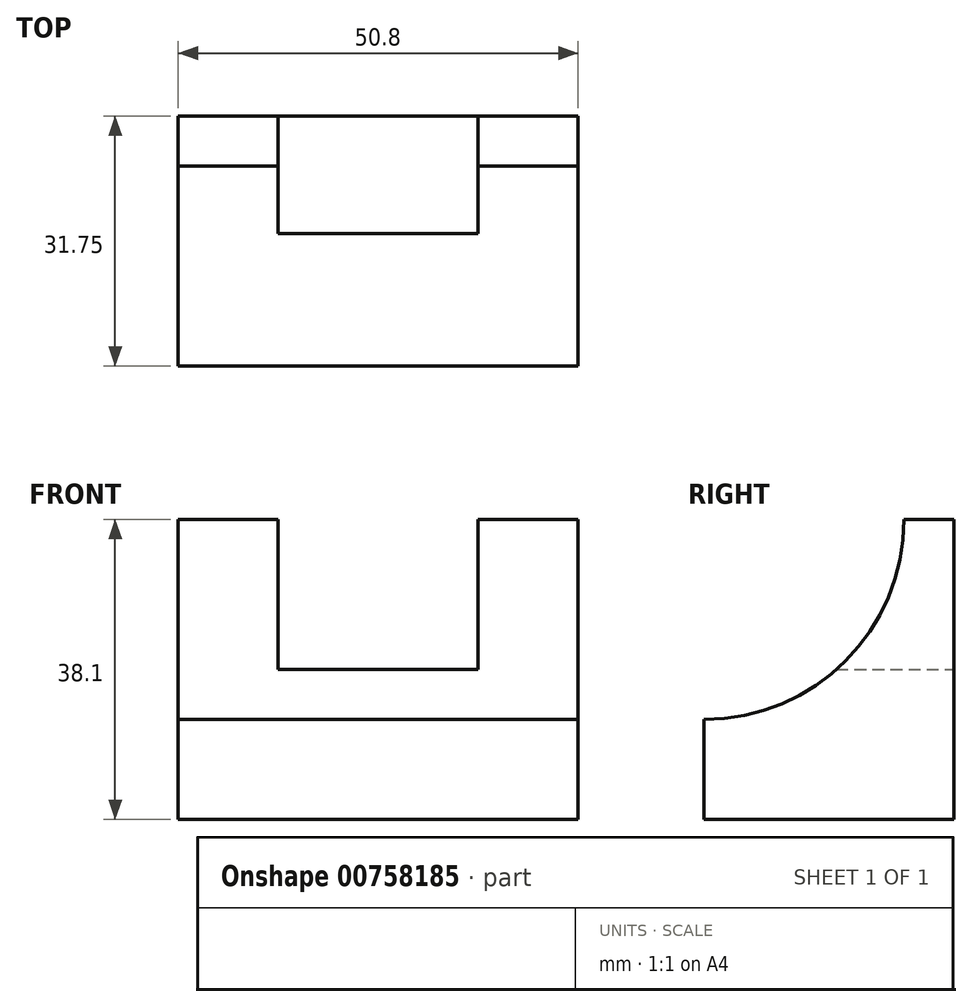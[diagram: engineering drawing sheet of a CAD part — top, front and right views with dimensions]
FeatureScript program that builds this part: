
annotation { "Feature Type Name" : "Feature", "Feature Type Description" : "" }
export const myFeature = defineFeature(function(context is Context, id is Id, definition is map)
    precondition{}
    {
        {
            var Q0;
            Q0=qCreatedBy(makeId("Front.planeOp"),FACE);
            var sketch = newSketch(context, id + "F0", { "sketchPlane" : qUnion([Q0])});
            skLineSegment(sketch, "E0", {"start": v(0, 0) * mm, "end": v(50.8, 0) * mm});
            skLineSegment(sketch, "E1", {"start": v(50.8, 0) * mm, "end": v(50.8, 38.1) * mm});
            skLineSegment(sketch, "E2", {"start": v(50.8, 38.1) * mm, "end": v(0, 38.1) * mm});
            skLineSegment(sketch, "E3", {"start": v(0, 38.1) * mm, "end": v(0, 0) * mm});
            skSolve(sketch);
        }
        {
            var Q0;
            Q0 = qSketchRegion(id + "F0", true);
            extrude(context, id + "F1", {"entities" : qUnion([Q0]), "oppositeDirection" : true, "depth" : 31.75 * mm, "offsetDistance" : 25.4 * mm});
        }
        {
            var Q0;
            Q0=makeQuery(id+"F1.opExtrude","SWEPT_FACE",FACE,{"disambiguationData":[OSD([sQuery(id+"F0.wireOp",EDGE,"E1")])]});
            var sketch = newSketch(context, id + "F2", { "sketchPlane" : qUnion([Q0])});
            skArc(sketch, "E4", {"start": v(0, 12.7) * mm, "mid": v(17.96, 20.14) * mm, "end": v(25.4, 38.1) * mm});
            skSolve(sketch);
        }
        {
            var Q0;
            Q0 = qSketchRegion(id + "F2", true);
            var Q1;
            {var subQ0=sQuery(id+"F2.wireOp",EDGE,"E4");Q1=makeQuery(id+"F2.imprint","IMPRINT",FACE,{"disambiguationData":[TD([[makeQuery(id+"F2.imprint","IMPRINT",EDGE,{"derivedFrom":subQ0}),1.0]])]});}
            extrude(context, id + "F3", {"entities" : qUnion([Q0, Q1]), "operationType" : NewBodyOperationType.REMOVE, "oppositeDirection" : true, "depth" : 50.8 * mm, "offsetDistance" : 25.4 * mm});
        }
        {
            var Q0;
            Q0=makeQuery(id+"F1.opExtrude","CAP_FACE",FACE,{"disambiguationData":[OSD([sQuery(id+"F0.wireOp",EDGE,"E0"),sQuery(id+"F0.wireOp",EDGE,"E1"),sQuery(id+"F0.wireOp",EDGE,"E2"),sQuery(id+"F0.wireOp",EDGE,"E3")])],"isStart":false});
            var sketch = newSketch(context, id + "F4", { "sketchPlane" : qUnion([Q0])});
            skLineSegment(sketch, "E5", {"start": v(-38.1, 38.1) * mm, "end": v(-38.1, 19.05) * mm});
            skLineSegment(sketch, "E6", {"start": v(-38.1, 19.05) * mm, "end": v(-12.7, 19.05) * mm});
            skLineSegment(sketch, "E7", {"start": v(-12.7, 19.05) * mm, "end": v(-12.7, 38.1) * mm});
            skSolve(sketch);
        }
        {
            var Q0;
            Q0 = qSketchRegion(id + "F4", true);
            var Q1;
            {var subQ0=sQuery(id+"F4.wireOp",EDGE,"E5");Q1=makeQuery(id+"F4.imprint","IMPRINT",FACE,{"disambiguationData":[TD([[makeQuery(id+"F4.imprint","IMPRINT",EDGE,{"derivedFrom":subQ0}),1.0]])]});}
            extrude(context, id + "F5", {"entities" : qUnion([Q0, Q1]), "operationType" : NewBodyOperationType.REMOVE, "oppositeDirection" : true, "depth" : 15.88 * mm, "offsetDistance" : 25.4 * mm});
        }
    });
